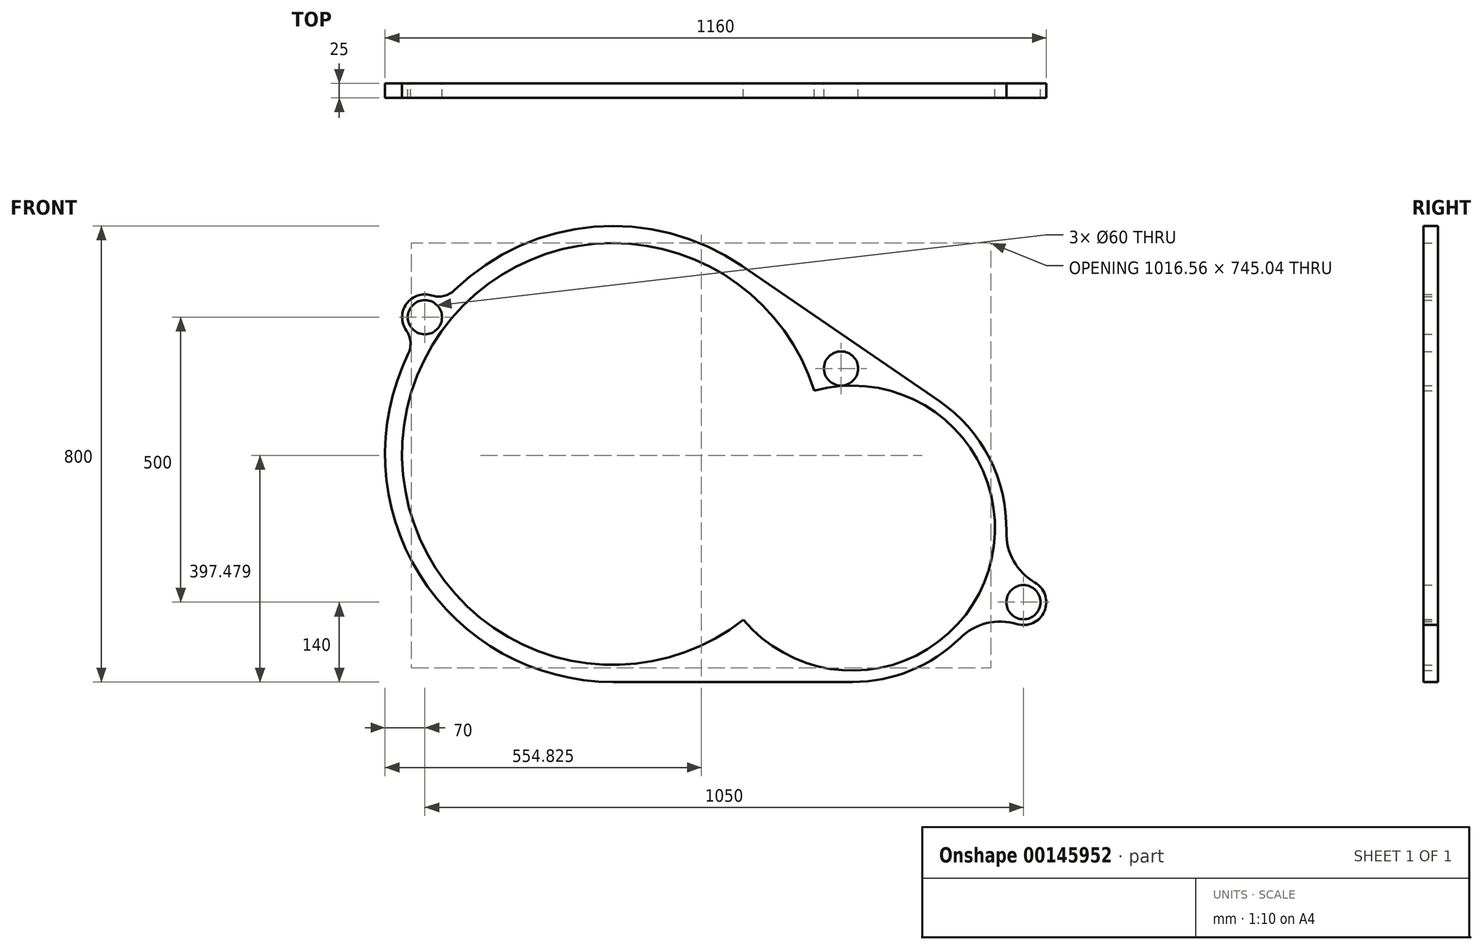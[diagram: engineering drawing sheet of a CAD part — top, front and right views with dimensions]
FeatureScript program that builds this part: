
annotation { "Feature Type Name" : "Feature", "Feature Type Description" : "" }
export const myFeature = defineFeature(function(context is Context, id is Id, definition is map)
    precondition{}
    {
        {
            var Q0;
            Q0=qCreatedBy(makeId("Front.planeOp"),FACE);
            var sketch = newSketch(context, id + "F0", { "sketchPlane" : qUnion([Q0])});
            skArc(sketch, "E0", {"start": v(353, 110.86) * mm, "mid": v(-353.46, 109.4) * mm, "end": v(228.65, -290.9) * mm});
            skArc(sketch, "E1", {"start": v(228.65, -290.9) * mm, "mid": v(658.82, -203.92) * mm, "end": v(353, 110.86) * mm});
            skArc(sketch, "E2", {"start": v(-359.22, 175.96) * mm, "mid": v(-339.4, -211.68) * mm, "end": v(0, -400) * mm});
            skCircle(sketch, "E3", {"center": v(-330, 240) * mm, "radius": 30 * mm});
            skCircle(sketch, "E4", {"center": v(720, -260) * mm, "radius": 30 * mm});
            skCircle(sketch, "E5", {"center": v(270, -37) * mm, "radius": 30 * mm});
            skCircle(sketch, "E6", {"center": v(400, 150) * mm, "radius": 30 * mm});
            skArc(sketch, "E7.trimOffspring", {"start": v(225.97, 330.06) * mm, "mid": v(-33.63, 398.58) * mm, "end": v(-278.08, 287.53) * mm});
            skArc(sketch, "E8.trimOffspring", {"start": v(420, -400) * mm, "mid": v(522.21, -379.9) * mm, "end": v(609.21, -322.61) * mm});
            skArc(sketch, "E9", {"start": v(-317.94, 278.14) * mm, "mid": v(-362.35, 263.53) * mm, "end": v(-362.57, 216.78) * mm});
            skArc(sketch, "E10", {"start": v(708.37, -298.27) * mm, "mid": v(756.7, -275.9) * mm, "end": v(739.97, -225.34) * mm});
            skLineSegment(sketch, "E11", {"start": v(225.97, 330.06) * mm, "end": v(572.53, 92.79) * mm});
            skLineSegment(sketch, "E12", {"start": v(0, -400) * mm, "end": v(420, -400) * mm});
            skArc(sketch, "E13", {"start": v(689.93, -136.35) * mm, "mid": v(702.73, -187.71) * mm, "end": v(739.97, -225.34) * mm});
            skArc(sketch, "E14", {"start": v(708.37, -298.27) * mm, "mid": v(655.45, -296.83) * mm, "end": v(609.21, -322.61) * mm});
            skArc(sketch, "E15", {"start": v(-317.94, 278.14) * mm, "mid": v(-296.72, 277.34) * mm, "end": v(-278.08, 287.53) * mm});
            skArc(sketch, "E16", {"start": v(-359.22, 175.96) * mm, "mid": v(-355.27, 196.83) * mm, "end": v(-362.57, 216.78) * mm});
            skArc(sketch, "E17.trimOffspring", {"start": v(689.93, -136.35) * mm, "mid": v(660.3, -6.89) * mm, "end": v(572.53, 92.79) * mm});
            skSolve(sketch);
        }
        {
            var Q0;
            Q0=makeQuery(id+"F0.imprint","IMPRINT",FACE,{"disambiguationData":[TD([[makeQuery(id+"F0.imprint","IMPRINT",EDGE,{"derivedFrom":sQuery(id+"F0.wireOp",EDGE,"E0")}),-1.0]])]});
            extrude(context, id + "F1", {"entities" : qUnion([Q0]), "depth" : 25 * mm});
        }
    });
